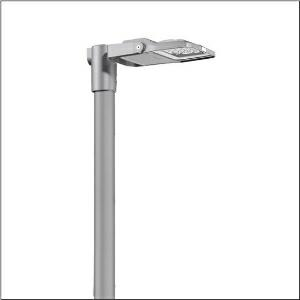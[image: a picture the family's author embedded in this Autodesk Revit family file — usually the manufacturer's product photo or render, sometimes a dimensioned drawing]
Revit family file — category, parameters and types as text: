
# Revit family: floodlight_fl_21_iq_micro___pl64_5xa7761a4e3a_8e2d
name_source: partatom
category: Lighting Fixtures
units: mm (PartAtom-declared; Revit-internal decimal feet)

## family parameters
Cut with Voids When Loaded = No
Host = Face
Light Source = No
Part Type = Normal
Room Calculation Point = No
Round Connector Dimension = Use Diameter
Shared = No

## types (1)
- --- (1 x LED, 2980 lm, 23.1 W, 4000K)
    Apparent Load = 23 VA
    CIE Flux Codes = 28 80 98 100 100
    Color Rendering = 70
    Color Temperature = 4000K
    Default Elevation = 1800 mm
    Description = Floodlight FL 21 iQ micro, floodlight, primary light control with lens, of PMMA, primary optical cover: protective disc, of toughened safety glass, transparent, light distribution: PL64, light emission: direct distribution, installation type: surface-mounted, LED, High Power LED, rated luminous flux: 2.980lm, luminous efficacy: 129lm/W, light colour: 740, colour temperature: 4000K, control gear: iQ Comfort/DALI, control: optimised constant luminous flux control (CLO 2.0), Desk-Remote (wireless, voltage-free reading and setting of iQ features in the workshop via application-optimized NFC function/RFID function), Light-Fading, Smart-Wire, Night-Set, Lumen-Switch, Temp-Guard, Auto-Match, with terminal, 6-pole, mains connection: 220..240V, AC, 50/60Hz, start of lifetime: 23W, end of service life: 24W, reduction: 11W, luminaire housing, of diecast aluminium, powder-coated, Siteco® metallic grey (DB 702S), corrosivity category C5 mid according to DIN EN ISO 12944, suitable for swimming pools, chlorine-resistant, sealing non-destructively replaceable, please order mast flange separately, mast bracket, of steel, galvanised, powder-coated, Siteco® metallic grey (DB 702S), protection rating (complete): IP66, insulation class (complete): insulation class II (safety insulation), certification: CE, ENEC, VDE, protection symbol: D, impact resistance: IK07, permissible operating ambient temperature: -40..+40°C, permissible operating ambient temperature for outdoor applications: -40..+50°C, standard: DIN EN 12944, LABS conformity tested according to VDMA 24364:2018-05, packaging unit: 1 piece

Light Distribution: PL64
    Height = 65 mm
    Lamp = 1 x LED
    Lamp Light Flux = 2980 lm
    Lamp Power = 23.1 W
    Lamp count = 1
    Length = 312 mm
    Luminous efficacy = 129 lm/W
    Manufacturer = Siteco
    ModVariant = No
    Model = 5XA7761A4E3A
    Number of Poles = 1
    OnlyDefault = Yes
    Power Factor = 1
    Product Name = Floodlight FL 21 iQ micro | PL64
    Product group = floodlight | pylon annexe
    ProductGroupID = 6201
    Protection Class = Protection class II
    Protection Degree = IP 66
    RLX_Detail_Level = 1
    RLX_Emergency_Light_Flux = 0 lm
    RLX_Emergency_Type = 0
    RLX_Emergency_Type_DB = No
    RlxData = <blob elided: 101757 chars, md5=4fb2bb9d>
    Socket = socket
    Standby Power = 0 W
    System Light Flux = 2980 lm
    System Power = 23 W
    Type Comments = factory setting: luminous flux: 100 % | dim-lin: 254 | 455 mA
    Type Image = l_1007121.jpg
    URL = http://relux.com
    VarID = @adj_202149
    Voltage = 0 V
    Weight = 0.00 kg
    Width = 230 mm

## geometry (parser evidence)
native form markers: Blend x4, Sweep x12
no freeform markers — native parametric forms only
